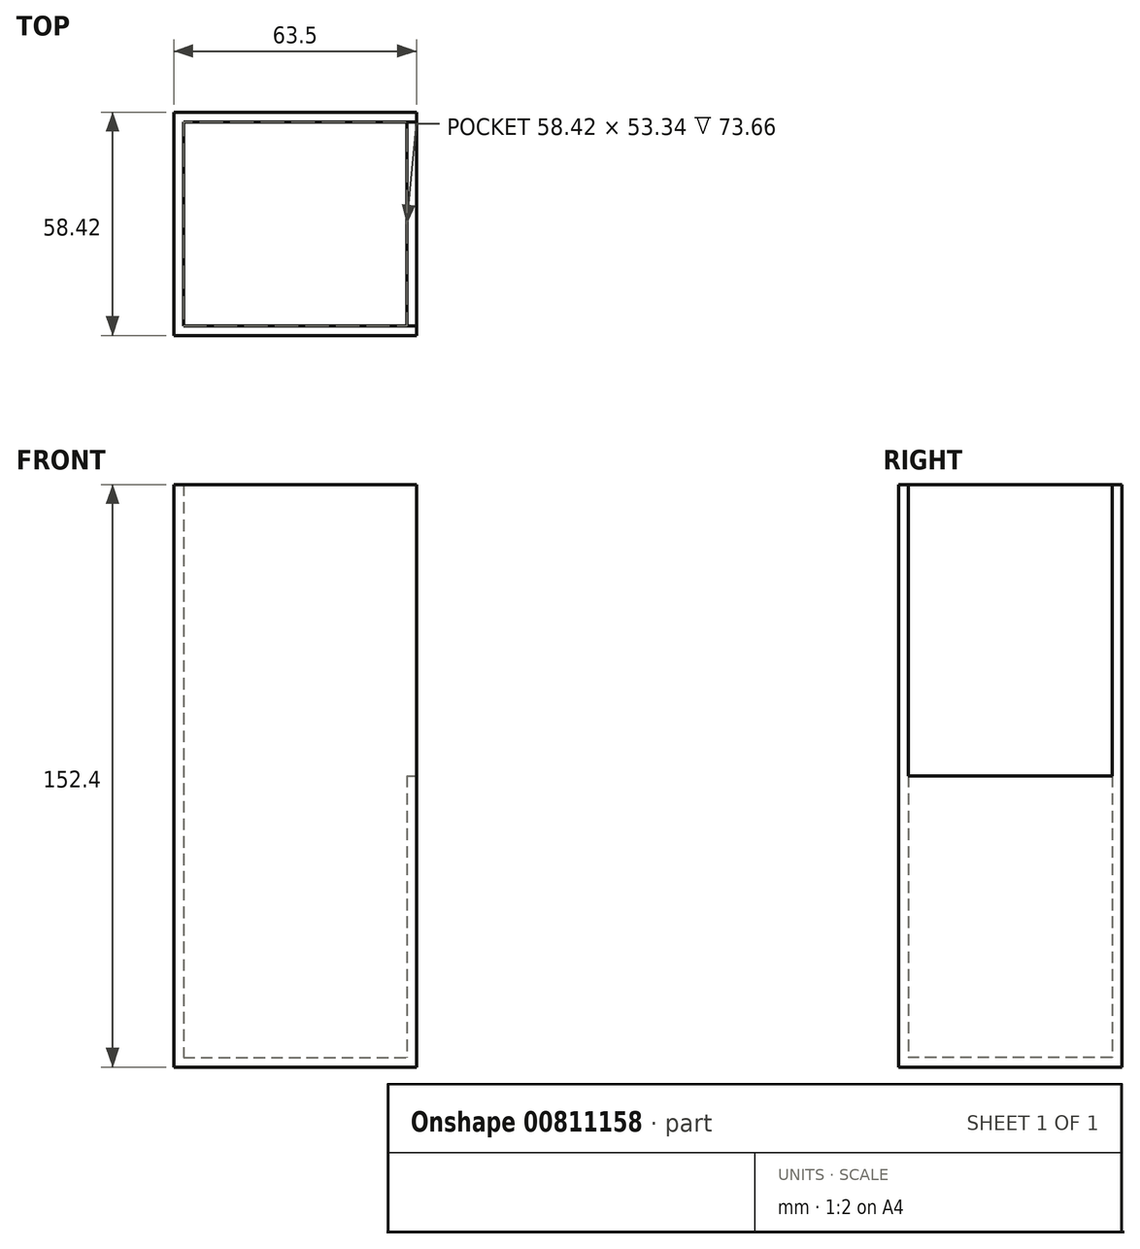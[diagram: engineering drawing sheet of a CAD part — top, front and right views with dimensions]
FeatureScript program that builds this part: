
annotation { "Feature Type Name" : "Feature", "Feature Type Description" : "" }
export const myFeature = defineFeature(function(context is Context, id is Id, definition is map)
    precondition{}
    {
        {
            var Q0;
            Q0=qCreatedBy(makeId("Front.planeOp"),FACE);
            var sketch = newSketch(context, id + "F0", { "sketchPlane" : qUnion([Q0])});
            skLineSegment(sketch, "E0.bottom", {"start": v(-31.75, 65.49) * mm, "end": v(31.75, 65.49) * mm});
            skLineSegment(sketch, "E0.top", {"start": v(-31.75, -86.91) * mm, "end": v(31.75, -86.91) * mm});
            skLineSegment(sketch, "E0.left", {"start": v(-31.75, 65.49) * mm, "end": v(-31.75, -86.91) * mm});
            skLineSegment(sketch, "E0.right", {"start": v(31.75, 65.49) * mm, "end": v(31.75, -86.91) * mm});
            skLineSegment(sketch, "E1", {"start": v(0, 76.03) * mm, "end": v(0, -105.47) * mm, "construction": true});
            skSolve(sketch);
        }
        {
            var Q0;
            Q0=makeQuery(id+"F0.imprint","IMPRINT",FACE,{"disambiguationData":[TD([[makeQuery(id+"F0.imprint","IMPRINT",EDGE,{"derivedFrom":sQuery(id+"F0.wireOp",EDGE,"E0.bottom")}),-1.0]])]});
            extrude(context, id + "F1", {"entities" : qUnion([Q0]), "oppositeDirection" : true, "depth" : 58.42 * mm, "offsetDistance" : 25.4 * mm});
        }
        {
            var Q0;
            Q0=makeQuery(id+"F1.opExtrude","SWEPT_FACE",FACE,{"disambiguationData":[OSD([sQuery(id+"F0.wireOp",EDGE,"E0.bottom")])]});
            shell(context, id + "F2", {"entities" : qUnion([Q0]), "thickness" : 2.54 * mm});
        }
        {
            var Q0;
            Q0=makeQuery(id+"F1.opExtrude","SWEPT_FACE",FACE,{"disambiguationData":[OSD([sQuery(id+"F0.wireOp",EDGE,"E0.right")])]});
            var sketch = newSketch(context, id + "F3", { "sketchPlane" : qUnion([Q0])});
            skLineSegment(sketch, "E2", {"start": v(29.2, 87.43) * mm, "end": v(29.21, -106.35) * mm, "construction": true});
            skLineSegment(sketch, "E3.bottom", {"start": v(2.54, 65.49) * mm, "end": v(55.88, 65.49) * mm});
            skLineSegment(sketch, "E3.top", {"start": v(2.54, -10.71) * mm, "end": v(55.88, -10.71) * mm});
            skLineSegment(sketch, "E3.left", {"start": v(2.54, 65.49) * mm, "end": v(2.54, -10.71) * mm});
            skLineSegment(sketch, "E3.right", {"start": v(55.88, 65.49) * mm, "end": v(55.88, -10.71) * mm});
            skSolve(sketch);
        }
        {
            var Q0;
            Q0 = qSketchRegion(id + "F3", true);
            extrude(context, id + "F4", {"entities" : qUnion([Q0]), "operationType" : NewBodyOperationType.REMOVE, "oppositeDirection" : true, "depth" : 25.4 * mm, "offsetDistance" : 25.4 * mm});
        }
    });
